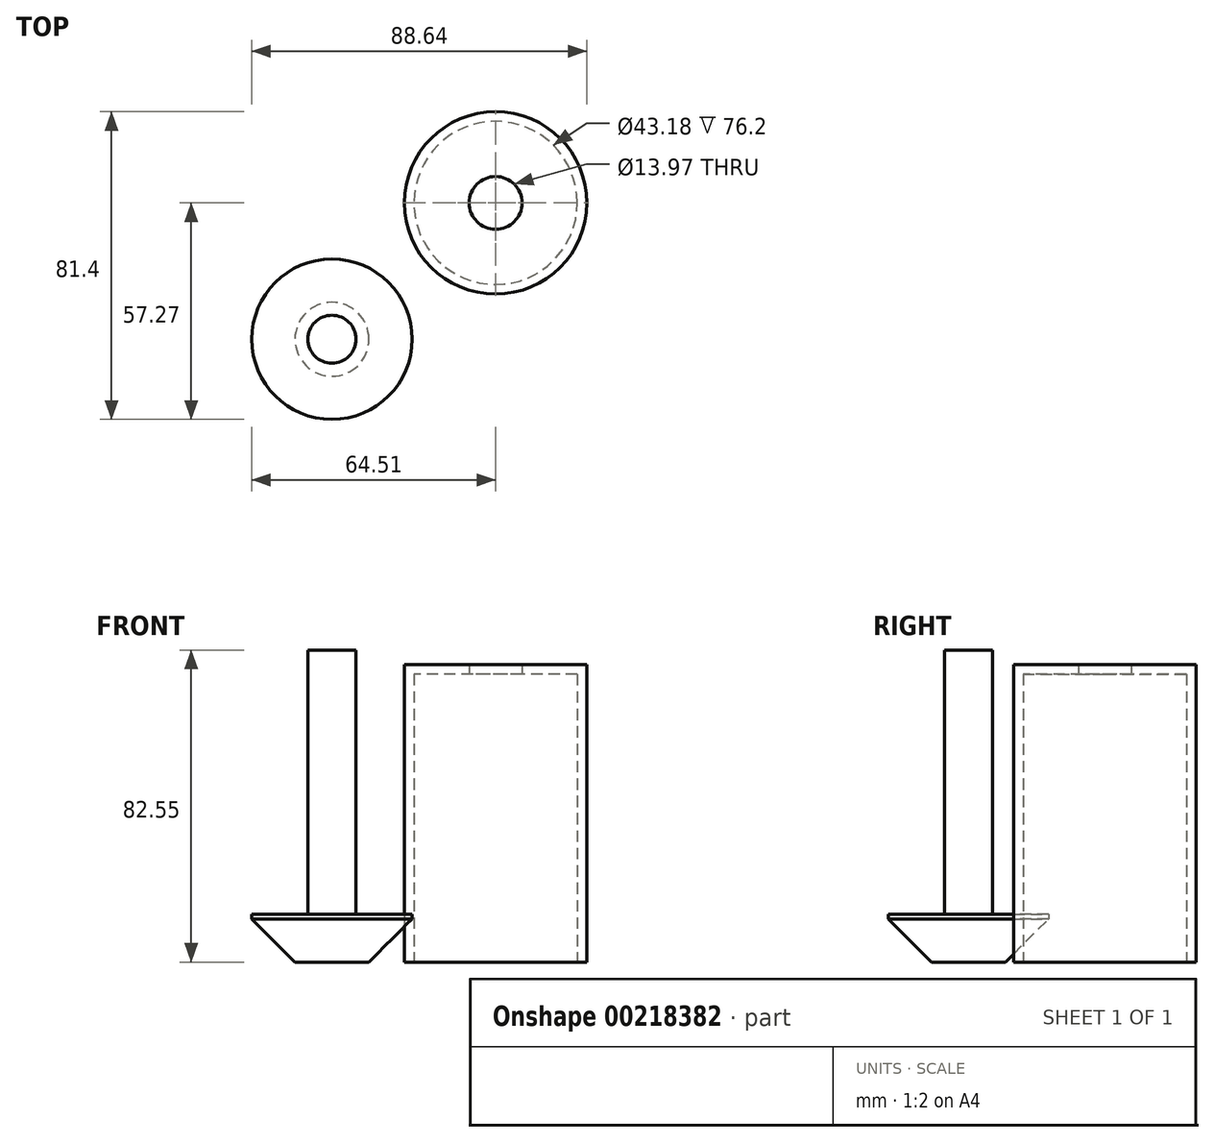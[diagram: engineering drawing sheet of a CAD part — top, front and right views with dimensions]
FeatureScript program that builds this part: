
annotation { "Feature Type Name" : "Feature", "Feature Type Description" : "" }
export const myFeature = defineFeature(function(context is Context, id is Id, definition is map)
    precondition{}
    {
        {
            var Q0;
            Q0=qCreatedBy(makeId("Top.planeOp"),FACE);
            var sketch = newSketch(context, id + "F0", { "sketchPlane" : qUnion([Q0])});
            skCircle(sketch, "E0", {"center": v(0, 0) * mm, "radius": 21.59 * mm});
            skCircle(sketch, "E1.0", {"center": v(0, 0) * mm, "radius": 24.13 * mm});
            skSolve(sketch);
        }
        {
            var Q0;
            Q0 = qSketchRegion(id + "F0", true);
            extrude(context, id + "F1", {"entities" : qUnion([Q0]), "depth" : 76.2 * mm});
        }
        {
            var Q0;
            Q0=qCreatedBy(makeId("Top.planeOp"),FACE);
            var sketch = newSketch(context, id + "F2", { "sketchPlane" : qUnion([Q0])});
            skCircle(sketch, "E2", {"center": v(-43.3, -36.06) * mm, "radius": 21.2 * mm});
            skSolve(sketch);
        }
        {
            var Q0;
            Q0 = qSketchRegion(id + "F2", true);
            extrude(context, id + "F3", {"entities" : qUnion([Q0]), "depth" : 12.7 * mm});
        }
        {
            var Q0;
            Q0=makeQuery(id+"F3.opExtrude","CAP_EDGE",EDGE,{"disambiguationData":[OSD([sQuery(id+"F2.wireOp",EDGE,"E2")])],"isStart":true});
            chamfer(context, id + "F4", {"entities" : qUnion([Q0]), "width" : 11.43 * mm, "tangentPropagation" : true});
        }
        {
            var Q0;
            Q0=makeQuery(id+"F3.opExtrude","CAP_FACE",FACE,{"disambiguationData":[OSD([sQuery(id+"F2.wireOp",EDGE,"E2")])],"isStart":false});
            var sketch = newSketch(context, id + "F5", { "sketchPlane" : qUnion([Q0])});
            skCircle(sketch, "E3", {"center": v(-43.3, -36.06) * mm, "radius": 6.35 * mm});
            skSolve(sketch);
        }
        {
            var Q0;
            Q0 = qSketchRegion(id + "F5", true);
            extrude(context, id + "F6", {"entities" : qUnion([Q0]), "operationType" : NewBodyOperationType.ADD, "depth" : 69.85 * mm});
        }
        {
            var Q0;
            Q0=makeQuery(id+"F1.opExtrude","CAP_FACE",FACE,{"disambiguationData":[OSD([sQuery(id+"F0.wireOp",EDGE,"E0"),sQuery(id+"F0.wireOp",EDGE,"E1.0")])],"isStart":false});
            var sketch = newSketch(context, id + "F7", { "sketchPlane" : qUnion([Q0])});
            skCircle(sketch, "E4", {"center": v(0, 0) * mm, "radius": 24.13 * mm});
            skCircle(sketch, "E5", {"center": v(0, 0) * mm, "radius": 6.99 * mm});
            skSolve(sketch);
        }
        {
            var Q0;
            Q0 = qSketchRegion(id + "F7", true);
            extrude(context, id + "F8", {"entities" : qUnion([Q0]), "operationType" : NewBodyOperationType.ADD, "depth" : 2.54 * mm});
        }
    });
